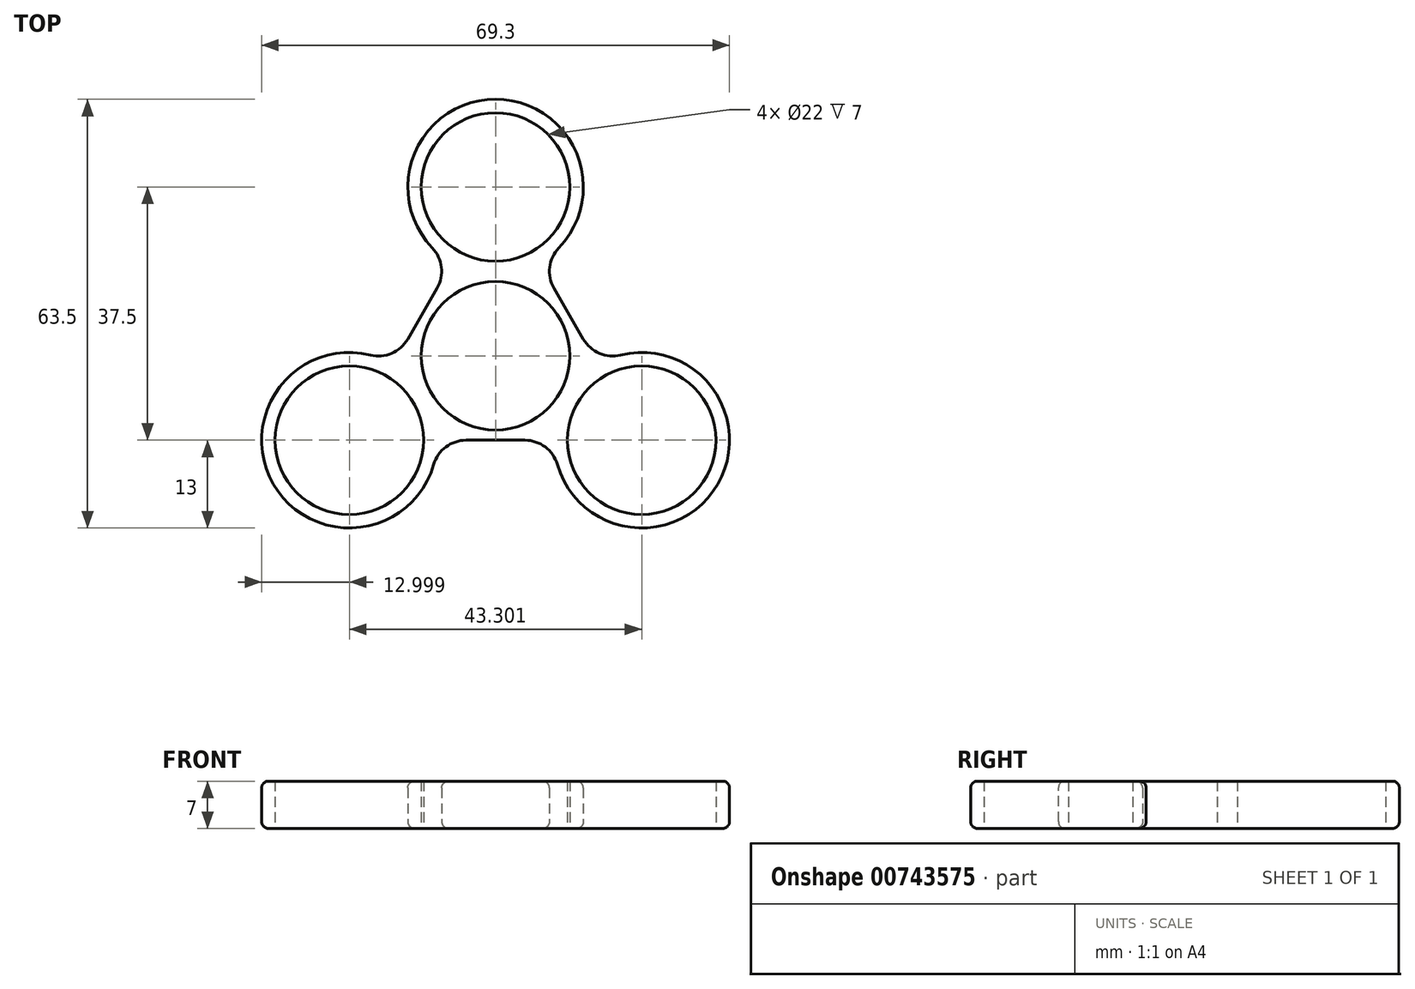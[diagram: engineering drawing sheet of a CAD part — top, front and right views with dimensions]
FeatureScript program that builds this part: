
annotation { "Feature Type Name" : "Feature", "Feature Type Description" : "" }
export const myFeature = defineFeature(function(context is Context, id is Id, definition is map)
    precondition{}
    {
        {
            var Q0;
            Q0=qCreatedBy(makeId("Top.planeOp"),FACE);
            var sketch = newSketch(context, id + "F0", { "sketchPlane" : qUnion([Q0])});
            skCircle(sketch, "E0", {"center": v(0, 0) * mm, "radius": 11 * mm});
            skLineSegment(sketch, "E1", {"start": v(0, 0) * mm, "end": v(0, 36.22) * mm, "construction": true});
            skLineSegment(sketch, "E2", {"start": v(0, 0) * mm, "end": v(-31.37, -18.11) * mm, "construction": true});
            skLineSegment(sketch, "E3", {"start": v(0, 0) * mm, "end": v(31.37, -18.11) * mm, "construction": true});
            skLineSegment(sketch, "E4", {"start": v(0, 36.22) * mm, "end": v(-31.37, -18.11) * mm, "construction": true});
            skLineSegment(sketch, "E5", {"start": v(31.37, -18.11) * mm, "end": v(-31.37, -18.11) * mm, "construction": true});
            skLineSegment(sketch, "E6", {"start": v(0, 36.22) * mm, "end": v(31.37, -18.11) * mm, "construction": true});
            skCircle(sketch, "E7.0", {"center": v(0, 0) * mm, "radius": 13 * mm});
            skPoint(sketch, "E8", {"position": v(-11.26, -6.5) * mm});
            skPoint(sketch, "E9", {"position": v(-21.65, -12.5) * mm});
            skPoint(sketch, "E10", {"position": v(0, 13) * mm});
            skPoint(sketch, "E11", {"position": v(0, 25) * mm});
            skPoint(sketch, "E12", {"position": v(11.26, -6.5) * mm});
            skPoint(sketch, "E13", {"position": v(21.65, -12.5) * mm});
            skCircle(sketch, "E14", {"center": v(-21.65, -12.5) * mm, "radius": 11 * mm});
            skCircle(sketch, "E15.0", {"center": v(-21.65, -12.5) * mm, "radius": 13 * mm});
            skCircle(sketch, "E16", {"center": v(0, 25) * mm, "radius": 11 * mm});
            skCircle(sketch, "E17.0", {"center": v(0, 25) * mm, "radius": 13 * mm});
            skCircle(sketch, "E18", {"center": v(21.65, -12.5) * mm, "radius": 11 * mm});
            skCircle(sketch, "E19.0", {"center": v(21.65, -12.5) * mm, "radius": 13 * mm});
            skLineSegment(sketch, "E20", {"start": v(0, 25) * mm, "end": v(-21.65, -12.5) * mm, "construction": true});
            skLineSegment(sketch, "E21", {"start": v(-21.65, -12.5) * mm, "end": v(21.65, -12.5) * mm, "construction": true});
            skLineSegment(sketch, "E22", {"start": v(21.65, -12.5) * mm, "end": v(0, 25) * mm, "construction": true});
            skLineSegment(sketch, "E23", {"start": v(-6.5, 13.74) * mm, "end": v(-15.15, -1.24) * mm});
            skLineSegment(sketch, "E24", {"start": v(-8.65, -12.5) * mm, "end": v(8.65, -12.5) * mm});
            skLineSegment(sketch, "E25", {"start": v(15.15, -1.24) * mm, "end": v(6.5, 13.74) * mm});
            skSolve(sketch);
        }
        {
            var Q0;
            Q0=makeQuery(id+"F0.imprint","IMPRINT",FACE,{"disambiguationData":[TD([[makeQuery(id+"F0.imprint","IMPRINT",EDGE,{"derivedFrom":sQuery(id+"F0.wireOp",EDGE,"E16")}),-1.0]])]});
            var Q1;
            {var subQ0=sQuery(id+"F0.wireOp",EDGE,"E23");var subQ1=sQuery(id+"F0.wireOp",EDGE,"E7.0");var subQ2=makeQuery(id+"F0.imprint","INTERSECT",VERTEX,{"derivedFrom":[subQ1,subQ0]});Q1=makeQuery(id+"F0.imprint","IMPRINT",FACE,{"disambiguationData":[TD([[makeQuery(id+"F0.imprint","IMPRINT",EDGE,{"disambiguationData":[TD([[subQ2,1.0]])],"derivedFrom":subQ1}),-1.0]])]});}
            var Q2;
            Q2=makeQuery(id+"F0.imprint","IMPRINT",FACE,{"disambiguationData":[TD([[makeQuery(id+"F0.imprint","IMPRINT",EDGE,{"derivedFrom":sQuery(id+"F0.wireOp",EDGE,"E0")}),-1.0]])]});
            var Q3;
            {var subQ0=sQuery(id+"F0.wireOp",EDGE,"E25");var subQ1=sQuery(id+"F0.wireOp",EDGE,"E7.0");var subQ2=makeQuery(id+"F0.imprint","INTERSECT",VERTEX,{"derivedFrom":[subQ1,subQ0]});Q3=makeQuery(id+"F0.imprint","IMPRINT",FACE,{"disambiguationData":[TD([[makeQuery(id+"F0.imprint","IMPRINT",EDGE,{"disambiguationData":[TD([[subQ2,-1.0]])],"derivedFrom":subQ1}),-1.0]])]});}
            var Q4;
            {var subQ0=sQuery(id+"F0.wireOp",EDGE,"E25");var subQ1=sQuery(id+"F0.wireOp",EDGE,"E7.0");var subQ2=makeQuery(id+"F0.imprint","INTERSECT",VERTEX,{"derivedFrom":[subQ1,subQ0]});Q4=makeQuery(id+"F0.imprint","IMPRINT",FACE,{"disambiguationData":[TD([[makeQuery(id+"F0.imprint","IMPRINT",EDGE,{"disambiguationData":[TD([[subQ2,1.0]])],"derivedFrom":subQ1}),-1.0]])]});}
            var Q5;
            Q5=makeQuery(id+"F0.imprint","IMPRINT",FACE,{"disambiguationData":[TD([[makeQuery(id+"F0.imprint","IMPRINT",EDGE,{"derivedFrom":sQuery(id+"F0.wireOp",EDGE,"E18")}),-1.0]])]});
            var Q6;
            {var subQ0=sQuery(id+"F0.wireOp",EDGE,"E24");var subQ1=sQuery(id+"F0.wireOp",EDGE,"E7.0");var subQ2=makeQuery(id+"F0.imprint","INTERSECT",VERTEX,{"derivedFrom":[subQ1,subQ0]});Q6=makeQuery(id+"F0.imprint","IMPRINT",FACE,{"disambiguationData":[TD([[makeQuery(id+"F0.imprint","IMPRINT",EDGE,{"disambiguationData":[TD([[subQ2,-1.0]])],"derivedFrom":subQ1}),-1.0]])]});}
            var Q7;
            {var subQ0=sQuery(id+"F0.wireOp",EDGE,"E24");var subQ1=sQuery(id+"F0.wireOp",EDGE,"E7.0");var subQ2=makeQuery(id+"F0.imprint","INTERSECT",VERTEX,{"derivedFrom":[subQ1,subQ0]});Q7=makeQuery(id+"F0.imprint","IMPRINT",FACE,{"disambiguationData":[TD([[makeQuery(id+"F0.imprint","IMPRINT",EDGE,{"disambiguationData":[TD([[subQ2,1.0]])],"derivedFrom":subQ1}),-1.0]])]});}
            var Q8;
            Q8=makeQuery(id+"F0.imprint","IMPRINT",FACE,{"disambiguationData":[TD([[makeQuery(id+"F0.imprint","IMPRINT",EDGE,{"derivedFrom":sQuery(id+"F0.wireOp",EDGE,"E14")}),-1.0]])]});
            var Q9;
            {var subQ0=sQuery(id+"F0.wireOp",EDGE,"E23");var subQ1=sQuery(id+"F0.wireOp",EDGE,"E7.0");var subQ2=makeQuery(id+"F0.imprint","INTERSECT",VERTEX,{"derivedFrom":[subQ1,subQ0]});Q9=makeQuery(id+"F0.imprint","IMPRINT",FACE,{"disambiguationData":[TD([[makeQuery(id+"F0.imprint","IMPRINT",EDGE,{"disambiguationData":[TD([[subQ2,-1.0]])],"derivedFrom":subQ1}),-1.0]])]});}
            var Q10;
            {var subQ0=sQuery(id+"F0.wireOp",EDGE,"E15.0");var subQ1=sQuery(id+"F0.wireOp",EDGE,"E7.0");var subQ2=makeQuery(id+"F0.imprint","INTERSECT",VERTEX,{"disambiguationData":[OD(0.0)],"derivedFrom":[subQ1,subQ0]});Q10=makeQuery(id+"F0.imprint","IMPRINT",FACE,{"disambiguationData":[TD([[makeQuery(id+"F0.imprint","IMPRINT",EDGE,{"disambiguationData":[TD([[subQ2,-1.0]])],"derivedFrom":subQ1}),1.0]])]});}
            var Q11;
            {var subQ0=sQuery(id+"F0.wireOp",EDGE,"E17.0");var subQ1=sQuery(id+"F0.wireOp",EDGE,"E7.0");var subQ2=makeQuery(id+"F0.imprint","INTERSECT",VERTEX,{"disambiguationData":[OD(0.0)],"derivedFrom":[subQ1,subQ0]});Q11=makeQuery(id+"F0.imprint","IMPRINT",FACE,{"disambiguationData":[TD([[makeQuery(id+"F0.imprint","IMPRINT",EDGE,{"disambiguationData":[TD([[subQ2,-1.0]])],"derivedFrom":subQ1}),1.0]])]});}
            var Q12;
            {var subQ0=sQuery(id+"F0.wireOp",EDGE,"E19.0");var subQ1=sQuery(id+"F0.wireOp",EDGE,"E7.0");var subQ2=makeQuery(id+"F0.imprint","INTERSECT",VERTEX,{"disambiguationData":[OD(0.0)],"derivedFrom":[subQ1,subQ0]});Q12=makeQuery(id+"F0.imprint","IMPRINT",FACE,{"disambiguationData":[TD([[makeQuery(id+"F0.imprint","IMPRINT",EDGE,{"disambiguationData":[TD([[subQ2,-1.0]])],"derivedFrom":subQ1}),1.0]])]});}
            extrude(context, id + "F1", {"entities" : qUnion([Q0, Q1, Q2, Q3, Q4, Q5, Q6, Q7, Q8, Q9, Q10, Q11, Q12]), "depth" : 7 * mm, "offsetDistance" : 25 * mm});
        }
        {
            var Q0;
            Q0=makeQuery(id+"F1.opExtrude","SWEPT_EDGE",EDGE,{"disambiguationData":[OSD([sQuery(id+"F0.wireOp",EDGE,"E19.0"),sQuery(id+"F0.wireOp",EDGE,"E25")])]});
            var Q1;
            Q1=makeQuery(id+"F1.opExtrude","SWEPT_EDGE",EDGE,{"disambiguationData":[OSD([sQuery(id+"F0.wireOp",EDGE,"E19.0"),sQuery(id+"F0.wireOp",EDGE,"E24")])]});
            var Q2;
            Q2=makeQuery(id+"F1.opExtrude","SWEPT_EDGE",EDGE,{"disambiguationData":[OSD([sQuery(id+"F0.wireOp",EDGE,"E15.0"),sQuery(id+"F0.wireOp",EDGE,"E24")])]});
            var Q3;
            Q3=makeQuery(id+"F1.opExtrude","SWEPT_EDGE",EDGE,{"disambiguationData":[OSD([sQuery(id+"F0.wireOp",EDGE,"E15.0"),sQuery(id+"F0.wireOp",EDGE,"E23")])]});
            var Q4;
            Q4=makeQuery(id+"F1.opExtrude","SWEPT_EDGE",EDGE,{"disambiguationData":[OSD([sQuery(id+"F0.wireOp",EDGE,"E17.0"),sQuery(id+"F0.wireOp",EDGE,"E23")])]});
            var Q5;
            Q5=makeQuery(id+"F1.opExtrude","SWEPT_EDGE",EDGE,{"disambiguationData":[OSD([sQuery(id+"F0.wireOp",EDGE,"E17.0"),sQuery(id+"F0.wireOp",EDGE,"E25")])]});
            fillet(context, id + "F2", {"entities" : qUnion([Q0, Q1, Q2, Q3, Q4, Q5]), "radius" : 5 * mm, "tangentPropagation" : true, "allowEdgeOverflow" : false});
        }
        {
            var Q0;
            Q0=makeQuery(id+"F1.opExtrude","CAP_EDGE",EDGE,{"disambiguationData":[OSD([sQuery(id+"F0.wireOp",EDGE,"E23")])],"isStart":false});
            var Q1;
            {var subQ0=sQuery(id+"F0.wireOp",EDGE,"E23");var subQ1=sQuery(id+"F0.wireOp",EDGE,"E15.0");Q1=makeQuery(id+"F2.opFillet","BLEND_EDGE",EDGE,{"blendedFrom":[makeQuery(id+"F1.opExtrude","SWEPT_EDGE",EDGE,{"disambiguationData":[OSD([subQ1,subQ0])]}),makeQuery(id+"F1.opExtrude","CAP_FACE",FACE,{"disambiguationData":[OSD([sQuery(id+"F0.wireOp",EDGE,"E0"),sQuery(id+"F0.wireOp",EDGE,"E14"),subQ1,sQuery(id+"F0.wireOp",EDGE,"E16"),sQuery(id+"F0.wireOp",EDGE,"E17.0"),sQuery(id+"F0.wireOp",EDGE,"E18"),sQuery(id+"F0.wireOp",EDGE,"E19.0"),subQ0,sQuery(id+"F0.wireOp",EDGE,"E24"),sQuery(id+"F0.wireOp",EDGE,"E25")])],"isStart":false})],"blendedInto":[makeQuery(id+"F1.opExtrude","CAP_FACE",FACE,{"disambiguationData":[OSD([sQuery(id+"F0.wireOp",EDGE,"E0"),sQuery(id+"F0.wireOp",EDGE,"E14"),subQ1,sQuery(id+"F0.wireOp",EDGE,"E16"),sQuery(id+"F0.wireOp",EDGE,"E17.0"),sQuery(id+"F0.wireOp",EDGE,"E18"),sQuery(id+"F0.wireOp",EDGE,"E19.0"),subQ0,sQuery(id+"F0.wireOp",EDGE,"E24"),sQuery(id+"F0.wireOp",EDGE,"E25")])],"isStart":false})]});}
            var Q2;
            Q2=makeQuery(id+"F1.opExtrude","CAP_EDGE",EDGE,{"disambiguationData":[OSD([sQuery(id+"F0.wireOp",EDGE,"E17.0")])],"isStart":true});
            var Q3;
            Q3=makeQuery(id+"F1.opExtrude","CAP_EDGE",EDGE,{"disambiguationData":[OSD([sQuery(id+"F0.wireOp",EDGE,"E17.0")])],"isStart":false});
            fillet(context, id + "F3", {"entities" : qUnion([Q0, Q1, Q2, Q3]), "radius" : 1 * mm, "tangentPropagation" : true, "allowEdgeOverflow" : false});
        }
    });
